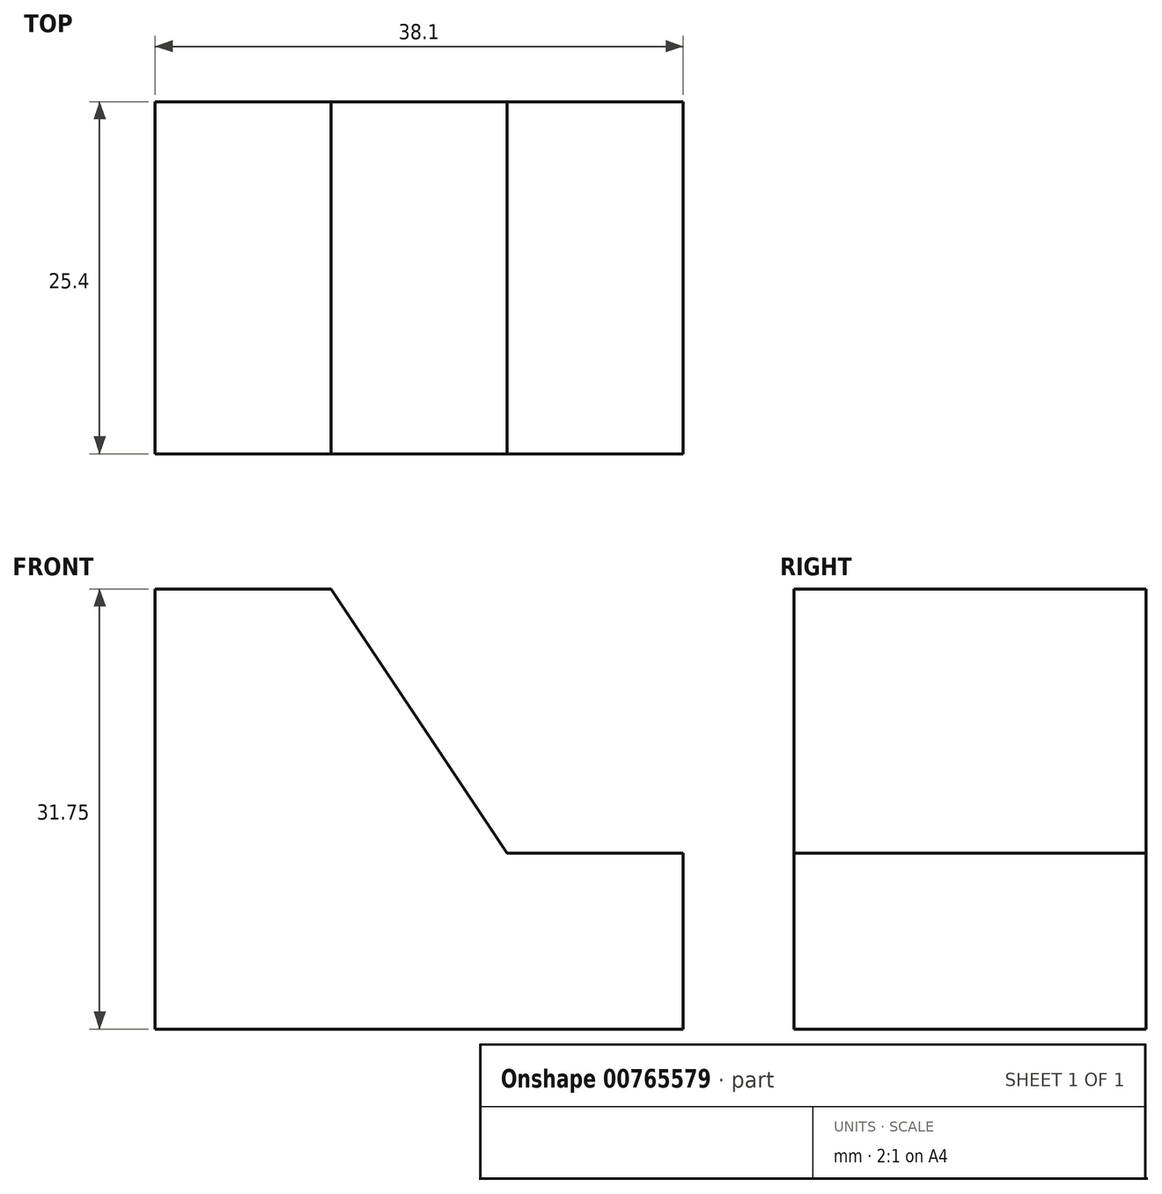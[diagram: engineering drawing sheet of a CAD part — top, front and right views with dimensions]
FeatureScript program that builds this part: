
annotation { "Feature Type Name" : "Feature", "Feature Type Description" : "" }
export const myFeature = defineFeature(function(context is Context, id is Id, definition is map)
    precondition{}
    {
        {
            var Q0;
            Q0=qCreatedBy(makeId("Front.planeOp"),FACE);
            var sketch = newSketch(context, id + "F0", { "sketchPlane" : qUnion([Q0])});
            skLineSegment(sketch, "E0", {"start": v(12.7, 31.75) * mm, "end": v(0, 31.75) * mm});
            skLineSegment(sketch, "E1", {"start": v(0, 31.75) * mm, "end": v(0, 0) * mm});
            skLineSegment(sketch, "E2", {"start": v(0, 0) * mm, "end": v(38.1, 0) * mm});
            skLineSegment(sketch, "E3", {"start": v(38.1, 0) * mm, "end": v(38.1, 12.7) * mm});
            skLineSegment(sketch, "E4", {"start": v(38.1, 12.7) * mm, "end": v(25.4, 12.7) * mm});
            skLineSegment(sketch, "E5", {"start": v(25.4, 12.7) * mm, "end": v(12.7, 31.75) * mm});
            skSolve(sketch);
        }
        {
            var Q0;
            Q0 = qSketchRegion(id + "F0", true);
            extrude(context, id + "F1", {"entities" : qUnion([Q0]), "depth" : 25.4 * mm, "offsetDistance" : 25.4 * mm});
        }
    });
